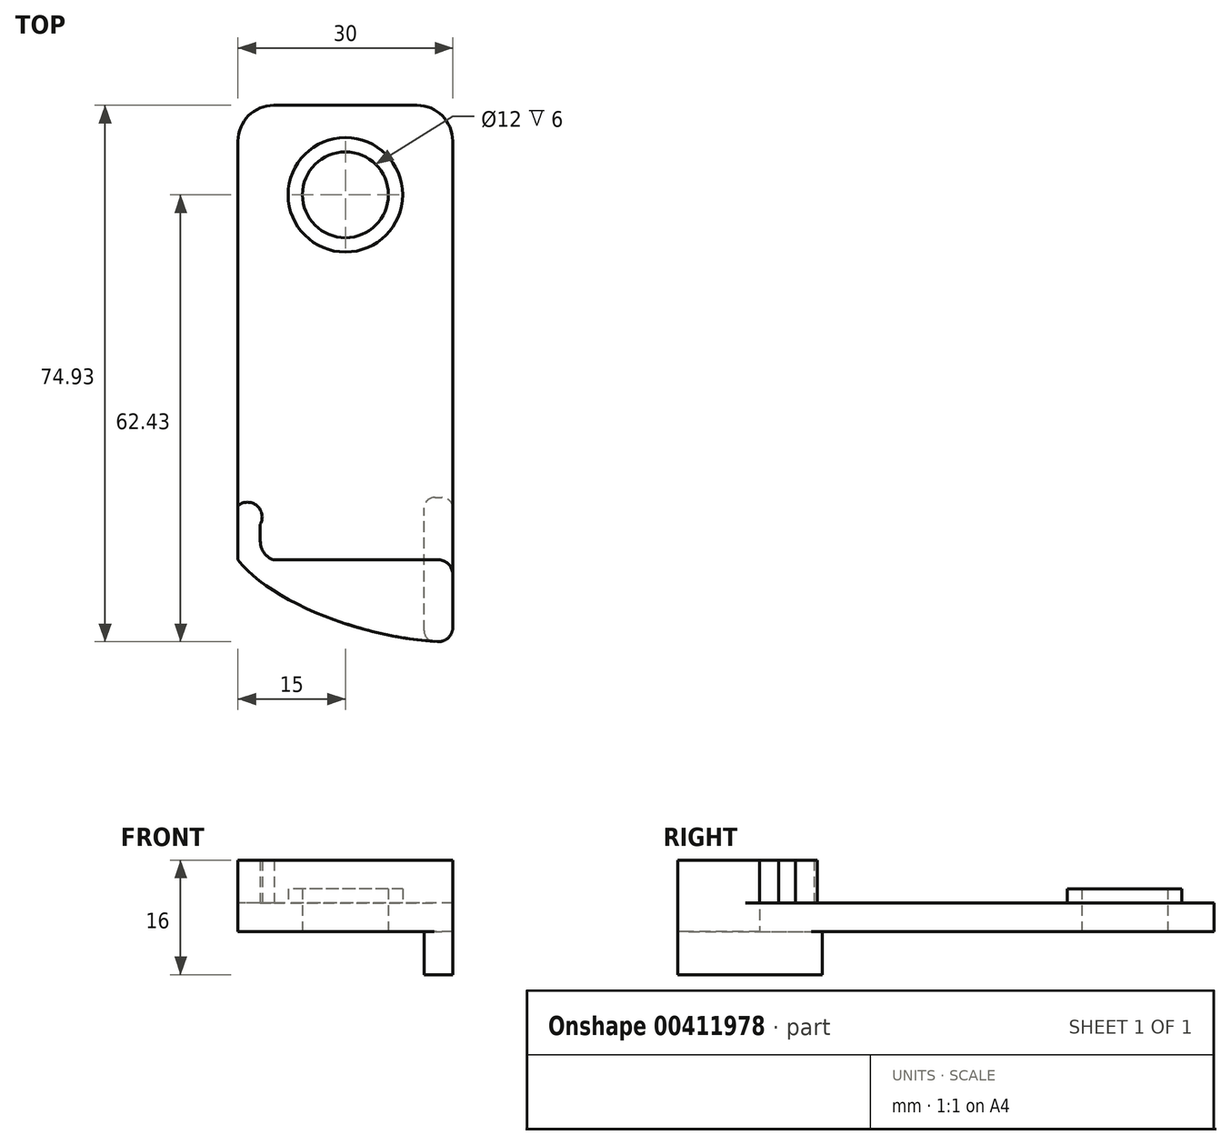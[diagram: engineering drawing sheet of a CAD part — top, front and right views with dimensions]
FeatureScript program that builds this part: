
annotation { "Feature Type Name" : "Feature", "Feature Type Description" : "" }
export const myFeature = defineFeature(function(context is Context, id is Id, definition is map)
    precondition{}
    {
        {
            var Q0;
            Q0=qCreatedBy(makeId("Top.planeOp"),FACE);
            var sketch = newSketch(context, id + "F0", { "sketchPlane" : qUnion([Q0])});
            skLineSegment(sketch, "E0.top", {"start": v(10, 37.5) * mm, "end": v(-10, 37.5) * mm});
            skLineSegment(sketch, "E0.left", {"start": v(15, -37.5) * mm, "end": v(15, 32.5) * mm});
            skLineSegment(sketch, "E0.right", {"start": v(-15, -26) * mm, "end": v(-15, 32.5) * mm});
            skPoint(sketch, "E0.middle", {"position": v(0, 0) * mm});
            skCircle(sketch, "E1", {"center": v(0, 25) * mm, "radius": 6 * mm});
            skCircle(sketch, "E2.0", {"center": v(0, 25) * mm, "radius": 8 * mm});
            skLineSegment(sketch, "E3", {"start": v(-9.96, -26) * mm, "end": v(15, -26) * mm});
            skPoint(sketch, "E4.visualSharp", {"position": v(-15, 37.5) * mm});
            skArc(sketch, "E4.filletArc", {"start": v(-10, 37.5) * mm, "mid": v(-13.54, 36.04) * mm, "end": v(-15, 32.5) * mm});
            skPoint(sketch, "E5.visualSharp", {"position": v(15, 37.5) * mm});
            skArc(sketch, "E5.filletArc", {"start": v(15, 32.5) * mm, "mid": v(13.54, 36.04) * mm, "end": v(10, 37.5) * mm});
            skFitSpline(sketch, "E6", {"points": [v(-15, -26) * mm, v(15, -37.5) * mm], "startDerivative": vector(14.12, -18.13) * mm, "endDerivative": vector(34.75, -0.31) * mm});
            skPoint(sketch, "E0.bottom.end.orphan", {"position": v(-15, -37.5) * mm});
            skLineSegment(sketch, "E7", {"start": v(-11.89, -21) * mm, "end": v(-11.89, -23.35) * mm});
            skFitSpline(sketch, "E8", {"points": [v(-11.89, -23.35) * mm, v(-11.65, -24.54) * mm, v(-11.03, -25.4) * mm, v(-9.96, -26) * mm], "startDerivative": vector(0.32, -5.94) * mm, "endDerivative": vector(3.17, -0.37) * mm});
            skLineSegment(sketch, "E9", {"start": v(-22.6, -21) * mm, "end": v(10.06, -21) * mm, "construction": true});
            skArc(sketch, "E10", {"start": v(-11.89, -21) * mm, "mid": v(-12.37, -18.42) * mm, "end": v(-15, -18.42) * mm});
            skSolve(sketch);
        }
        {
            var Q0;
            {var subQ1=sQuery(id+"F0.wireOp",EDGE,"E3");Q0=makeQuery(id+"F0.imprint","IMPRINT",FACE,{"disambiguationData":[TD([[makeQuery(id+"F0.imprint","IMPRINT",EDGE,{"derivedFrom":subQ1}),-1.0]])]});}
            extrude(context, id + "F1", {"entities" : qUnion([Q0]), "depth" : 10 * mm});
        }
        {
            var Q0;
            Q0=makeQuery(id+"F0.imprint","IMPRINT",FACE,{"disambiguationData":[TD([[makeQuery(id+"F0.imprint","IMPRINT",EDGE,{"derivedFrom":sQuery(id+"F0.wireOp",EDGE,"E0.top")}),1.0]])]});
            extrude(context, id + "F2", {"entities" : qUnion([Q0]), "depth" : 4 * mm});
        }
        {
            var Q0;
            Q0=makeQuery(id+"F0.imprint","IMPRINT",FACE,{"disambiguationData":[TD([[makeQuery(id+"F0.imprint","IMPRINT",EDGE,{"derivedFrom":sQuery(id+"F0.wireOp",EDGE,"E1")}),-1.0]])]});
            extrude(context, id + "F3", {"entities" : qUnion([Q0]), "operationType" : NewBodyOperationType.ADD, "depth" : 6 * mm});
        }
        {
            var Q0;
            Q0=makeQuery(id+"F2.opExtrude","SWEPT_BODY",BODY,{"disambiguationData":[OSD([sQuery(id+"F0.wireOp",EDGE,"E0.top"),sQuery(id+"F0.wireOp",EDGE,"E0.left"),sQuery(id+"F0.wireOp",EDGE,"E0.right"),sQuery(id+"F0.wireOp",EDGE,"E2.0"),sQuery(id+"F0.wireOp",EDGE,"E3"),sQuery(id+"F0.wireOp",EDGE,"E4.filletArc"),sQuery(id+"F0.wireOp",EDGE,"E5.filletArc"),sQuery(id+"F0.wireOp",EDGE,"E7"),sQuery(id+"F0.wireOp",EDGE,"E8"),sQuery(id+"F0.wireOp",EDGE,"JDLwIv78-LX44-XHO9-yHuR-osuizL2rWNrt")])]});
            var Q1;
            Q1=makeQuery(id+"F1.opExtrude","SWEPT_BODY",BODY,{"disambiguationData":[OSD([sQuery(id+"F0.wireOp",EDGE,"E0.left"),sQuery(id+"F0.wireOp",EDGE,"E0.right"),sQuery(id+"F0.wireOp",EDGE,"E3"),sQuery(id+"F0.wireOp",EDGE,"E6"),sQuery(id+"F0.wireOp",EDGE,"E7"),sQuery(id+"F0.wireOp",EDGE,"E8"),sQuery(id+"F0.wireOp",EDGE,"JDLwIv78-LX44-XHO9-yHuR-osuizL2rWNrt")])]});
            booleanBodies(context, id + "F4", {"operationType" : BooleanOperationType.UNION, "tools" : qUnion([Q0, Q1])});
        }
        {
            var Q0;
            Q0=makeQuery(id+"F1.opExtrude","SWEPT_EDGE",EDGE,{"disambiguationData":[OSD([sQuery(id+"F0.wireOp",EDGE,"E0.left"),sQuery(id+"F0.wireOp",EDGE,"E3")])]});
            var Q1;
            Q1=makeQuery(id+"F1.opExtrude","SWEPT_EDGE",EDGE,{"disambiguationData":[OSD([sQuery(id+"F0.wireOp",EDGE,"E0.left"),sQuery(id+"F0.wireOp",EDGE,"E6")])]});
            fillet(context, id + "F5", {"entities" : qUnion([Q0, Q1]), "radius" : 2 * mm, "tangentPropagation" : true, "allowEdgeOverflow" : false});
        }
        {
            var Q0;
            {var subQ0=sQuery(id+"F0.wireOp",EDGE,"E2.0");var subQ1=sQuery(id+"F0.wireOp",EDGE,"E10");var subQ2=sQuery(id+"F0.wireOp",EDGE,"E8");var subQ3=sQuery(id+"F0.wireOp",EDGE,"E7");var subQ4=sQuery(id+"F0.wireOp",EDGE,"E3");var subQ5=sQuery(id+"F0.wireOp",EDGE,"E0.right");var subQ6=sQuery(id+"F0.wireOp",EDGE,"E0.left");Q0=makeQuery(id+"F4.opBoolean","MERGE",FACE,{"derivedFrom":[makeQuery(id+"F1.opExtrude","CAP_FACE",FACE,{"disambiguationData":[OSD([subQ6,subQ5,subQ4,sQuery(id+"F0.wireOp",EDGE,"E6"),subQ3,subQ2,subQ1])],"isStart":true}),makeQuery(id+"F3.boolean.opBoolean","MERGE",FACE,{"derivedFrom":[makeQuery(id+"F2.opExtrude","CAP_FACE",FACE,{"disambiguationData":[OSD([sQuery(id+"F0.wireOp",EDGE,"E0.top"),subQ6,subQ5,subQ0,subQ4,sQuery(id+"F0.wireOp",EDGE,"E4.filletArc"),sQuery(id+"F0.wireOp",EDGE,"E5.filletArc"),subQ3,subQ2,subQ1])],"isStart":true}),makeQuery(id+"F3.opExtrude","CAP_FACE",FACE,{"disambiguationData":[OSD([sQuery(id+"F0.wireOp",EDGE,"E1"),subQ0])],"isStart":true})]})]});}
            var sketch = newSketch(context, id + "F6", { "sketchPlane" : qUnion([Q0])});
            skLineSegment(sketch, "E11", {"start": v(11, 37.27) * mm, "end": v(11, 17.27) * mm});
            skLineSegment(sketch, "E12", {"start": v(11, 17.27) * mm, "end": v(15, 17.27) * mm});
            skSolve(sketch);
        }
        {
            var Q0;
            {var subQ11=sQuery(id+"F6.wireOp",EDGE,"E11");Q0=makeQuery(id+"F6.imprint","IMPRINT",FACE,{"disambiguationData":[TD([[makeQuery(id+"F6.imprint","IMPRINT",EDGE,{"derivedFrom":subQ11}),1.0]])]});}
            extrude(context, id + "F7", {"entities" : qUnion([Q0]), "operationType" : NewBodyOperationType.ADD, "depth" : 6 * mm});
        }
        {
            var Q0;
            Q0=makeQuery(id+"F7.opExtrude","SWEPT_EDGE",EDGE,{"disambiguationData":[OSD([sQuery(id+"F6.wireOp",EDGE,"E11"),sQuery(id+"F6.wireOp",EDGE,"E12")])]});
            var Q1;
            Q1=makeQuery(id+"F7.opExtrude","SWEPT_EDGE",EDGE,{"disambiguationData":[OSD([sQuery(id+"F0.wireOp",EDGE,"E0.left"),sQuery(id+"F6.wireOp",EDGE,"E12")])]});
            var Q2;
            Q2=makeQuery(id+"F7.opExtrude","SWEPT_EDGE",EDGE,{"disambiguationData":[OSD([sQuery(id+"F0.wireOp",EDGE,"E6"),sQuery(id+"F6.wireOp",EDGE,"E11")])]});
            fillet(context, id + "F8", {"entities" : qUnion([Q0, Q1, Q2]), "radius" : 1.5 * mm, "tangentPropagation" : true, "allowEdgeOverflow" : false});
        }
    });
